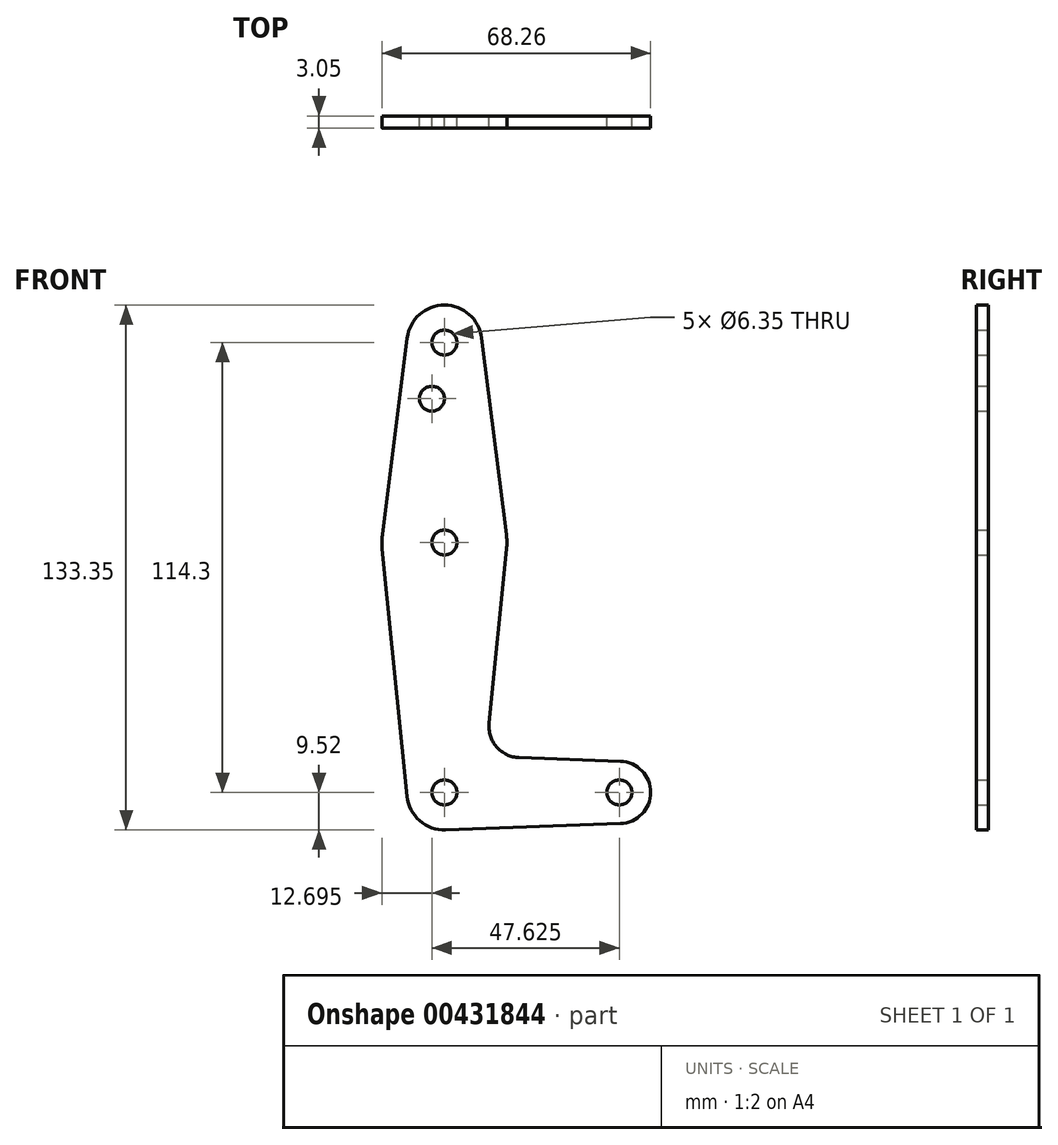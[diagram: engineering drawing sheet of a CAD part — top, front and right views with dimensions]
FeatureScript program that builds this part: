
annotation { "Feature Type Name" : "Feature", "Feature Type Description" : "" }
export const myFeature = defineFeature(function(context is Context, id is Id, definition is map)
    precondition{}
    {
        {
            var Q0;
            Q0=qCreatedBy(makeId("Front.planeOp"),FACE);
            var sketch = newSketch(context, id + "F0", { "sketchPlane" : qUnion([Q0])});
            skCircle(sketch, "E0", {"center": v(0, 0) * mm, "radius": 9.53 * mm});
            skCircle(sketch, "E1", {"center": v(44.45, 0) * mm, "radius": 7.94 * mm});
            skCircle(sketch, "E2", {"center": v(0, 63.5) * mm, "radius": 15.88 * mm});
            skCircle(sketch, "E3", {"center": v(0, 114.3) * mm, "radius": 9.53 * mm});
            skLineSegment(sketch, "E4", {"start": v(0, 114.3) * mm, "end": v(0, 0) * mm, "construction": true});
            skLineSegment(sketch, "E5", {"start": v(0, 0) * mm, "end": v(44.45, 0) * mm, "construction": true});
            skLineSegment(sketch, "E6", {"start": v(-9.45, 115.5) * mm, "end": v(-15.75, 65.48) * mm});
            skLineSegment(sketch, "E7", {"start": v(-9.48, -0.95) * mm, "end": v(-15.8, 61.91) * mm});
            skLineSegment(sketch, "E8", {"start": v(11.34, 17.6) * mm, "end": v(15.8, 61.91) * mm});
            skLineSegment(sketch, "E9", {"start": v(15.75, 65.48) * mm, "end": v(9.45, 115.5) * mm});
            skLineSegment(sketch, "E10", {"start": v(0.34, -9.52) * mm, "end": v(44.73, -7.93) * mm});
            skLineSegment(sketch, "E11", {"start": v(44.73, 7.93) * mm, "end": v(18.97, 8.85) * mm});
            skCircle(sketch, "E12", {"center": v(0, 114.3) * mm, "radius": 3.18 * mm});
            skCircle(sketch, "E13", {"center": v(0, 0) * mm, "radius": 3.18 * mm});
            skCircle(sketch, "E14", {"center": v(44.45, 0) * mm, "radius": 3.18 * mm});
            skCircle(sketch, "E15", {"center": v(0, 63.5) * mm, "radius": 3.18 * mm});
            skCircle(sketch, "E16", {"center": v(-3.18, 100.03) * mm, "radius": 3.18 * mm});
            skArc(sketch, "E17.filletArc", {"start": v(11.34, 17.6) * mm, "mid": v(13.26, 11.57) * mm, "end": v(18.97, 8.85) * mm});
            skSolve(sketch);
        }
        {
            var Q0;
            Q0 = qSketchRegion(id + "F0", true);
            extrude(context, id + "F1", {"entities" : qUnion([Q0]), "depth" : 3.05 * mm});
        }
    });
